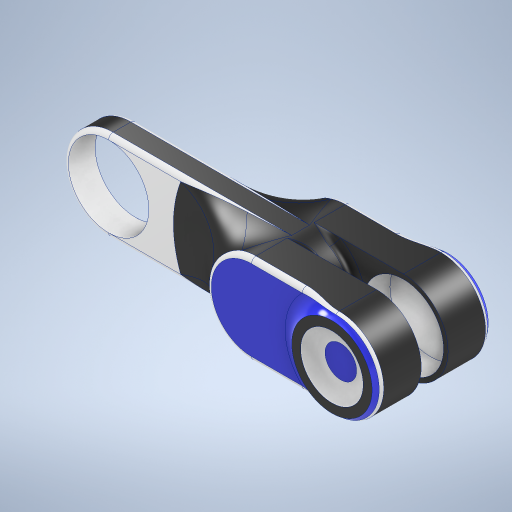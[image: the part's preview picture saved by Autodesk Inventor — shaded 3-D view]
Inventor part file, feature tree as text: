
AUTODESK INVENTOR PART (.ipt)
format: ipt  version: 2024 (Build 280153000, 153)  size: 565,760 bytes
history: native  units: mm
features: sketch x6, extrude x5, fillet x4, mirror x1
ambient origin geometry x8: Origin, YZ Plane, XZ Plane, XY Plane, X Axis, Y Axis, Z Axis, Center Point
bodies: Solid1 (feature_tree)
feature tree (16):
  extrude  "Extrusion1"  Depth=100.0mm
  extrude  "Extrusion2"  Depth=200.0mm
  extrude  "Extrusion3"  Depth=100.0mm TaperAngle=0.0deg
  fillet  "Fillet2"  Radius=100.0mm
  extrude  "Extrusion4"  Depth=90.0mm
  fillet  "Fillet3"  Radius=40.0mm
  mirror  "Mirror1"
  fillet  "Fillet6"  Radius=90.0mm
  fillet  "Fillet7"  Radius=70.0mm
  sketch  "Sketch9"  dims[d41=10.0mm d42=0.0mm d43=20.0mm]
  extrude  "Extrusion5"  Depth=20.0mm
  sketch  "Sketch5"  dims[d25=90.0mm d26=100.0mm]
  sketch  "Sketch6"  dims[d27=200.0mm d28=200.0mm]
  sketch  "Sketch7"  dims[d29=50.0mm d30=15.0mm d31=0.0mm d32=100.0mm]
  sketch  "Sketch8"  dims[d34=100.0mm d35=50.0mm d36=40.0mm d37=0.0mm d39=90.0mm d40=70.0mm]
  sketch  "Sketch10"  dims[d44=90.0mm d45=30.0mm d46=0.0mm d47=5.0mm d50=8.0mm d51=100.0mm d53=14.0mm d54=12.0mm d55=20.0mm d56=2.5mm d57=2.5mm d58=100.0mm d59=0.0mm]
